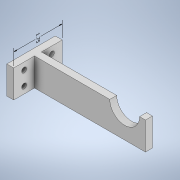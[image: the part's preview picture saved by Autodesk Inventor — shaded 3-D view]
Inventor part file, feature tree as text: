
AUTODESK INVENTOR PART (.ipt)
format: ipt  version: 2021.1 (Build 251245000, 245)  size: 139,264 bytes
history: native  units: in
note: dims shown in document units (in); Inventor stores cm internally (conversion verified against a paired STEP export)
features: sketch x3, other x2, extrude x2, hole x1, mirror x1, plane x1
ambient origin geometry x8: Origin, YZ Plane, XZ Plane, XY Plane, X Axis, Y Axis, Z Axis, Center Point
bodies: Solid1 (feature_tree)
feature tree (10):
  other  "Annotations"
  extrude  "Extrusion1"  Depth=1.0in
  extrude  "Extrusion2"  Depth=3.5in
  hole  "Hole1"  [1 undecoded]
  mirror  "Mirror1"
  sketch  "Sketch2"  dims[d0=4.25in d1=1.0in]
  sketch  "Sketch3"  dims[d2=1.075in d3=3.5in]
  sketch  "Sketch4"  dims[d4=0.25in d5=0.0in d6=1.75in d7=0.0in d8=0.25in d9=0.25in d10=0.177in d11=0.75in d12=0.313in d13=0.164in d14=0.5635in d15=1.0in d16=0.8108in d17=0.25in d18=1.75in]
  plane  "Work Plane1"
  other  "Linear Dimension 1"
note: 1 required parameter value undecoded (feature->parameter linkage not recoverable at this tier; creation-order binding heuristic only, values carry confidence <= 0.55)
